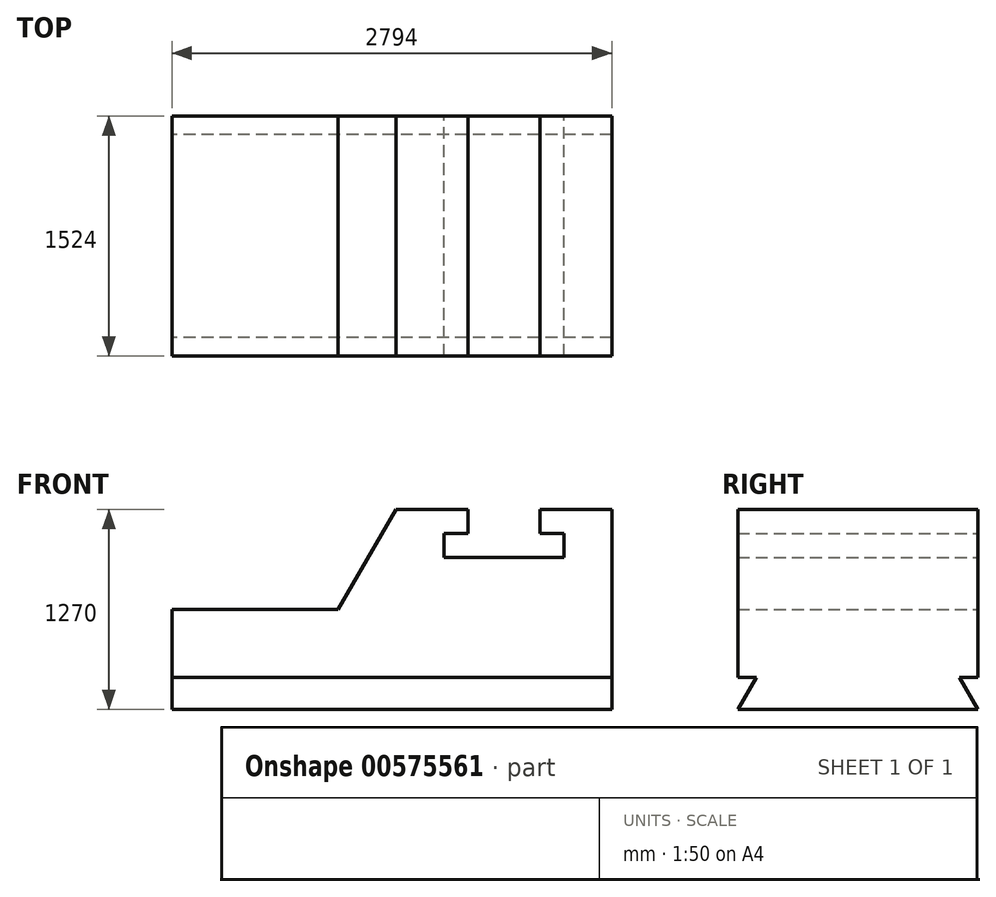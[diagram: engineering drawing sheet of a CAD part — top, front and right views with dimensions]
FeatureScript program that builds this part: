
annotation { "Feature Type Name" : "Feature", "Feature Type Description" : "" }
export const myFeature = defineFeature(function(context is Context, id is Id, definition is map)
    precondition{}
    {
        {
            var Q0;
            Q0=qCreatedBy(makeId("Front.planeOp"),FACE);
            var sketch = newSketch(context, id + "F0", { "sketchPlane" : qUnion([Q0])});
            skLineSegment(sketch, "E0", {"start": v(-53.89, -19.32) * mm, "end": v(2740.11, -19.32) * mm});
            skLineSegment(sketch, "E1", {"start": v(2740.11, -19.32) * mm, "end": v(2740.11, 1250.68) * mm});
            skLineSegment(sketch, "E2", {"start": v(2740.11, 1250.68) * mm, "end": v(2282.91, 1250.68) * mm});
            skLineSegment(sketch, "E3", {"start": v(2282.91, 1250.68) * mm, "end": v(2282.91, 1098.28) * mm});
            skLineSegment(sketch, "E4", {"start": v(2282.91, 1098.28) * mm, "end": v(2435.31, 1098.28) * mm});
            skLineSegment(sketch, "E5", {"start": v(2435.31, 1098.28) * mm, "end": v(2435.31, 945.88) * mm});
            skLineSegment(sketch, "E6", {"start": v(2435.31, 945.88) * mm, "end": v(1673.31, 945.88) * mm});
            skLineSegment(sketch, "E7", {"start": v(1673.31, 945.88) * mm, "end": v(1673.31, 1098.28) * mm});
            skLineSegment(sketch, "E8", {"start": v(1673.31, 1098.28) * mm, "end": v(1825.71, 1098.28) * mm});
            skLineSegment(sketch, "E9", {"start": v(1825.71, 1098.28) * mm, "end": v(1825.71, 1250.68) * mm});
            skLineSegment(sketch, "E10", {"start": v(1825.71, 1250.68) * mm, "end": v(1368.51, 1250.68) * mm});
            skLineSegment(sketch, "E11", {"start": v(-53.89, -19.32) * mm, "end": v(-53.89, 615.68) * mm});
            skLineSegment(sketch, "E12", {"start": v(1368.51, 1250.68) * mm, "end": v(1001.9, 615.68) * mm});
            skLineSegment(sketch, "E13", {"start": v(-53.89, 615.68) * mm, "end": v(1001.9, 615.68) * mm});
            skSolve(sketch);
        }
        {
            var Q0;
            Q0 = qSketchRegion(id + "F0", true);
            extrude(context, id + "F1", {"entities" : qUnion([Q0]), "depth" : 1524 * mm, "offsetDistance" : 25.4 * mm});
        }
        {
            var Q0;
            Q0=makeQuery(id+"F1.opExtrude","SWEPT_FACE",FACE,{"disambiguationData":[OSD([sQuery(id+"F0.wireOp",EDGE,"E11")])]});
            var sketch = newSketch(context, id + "F2", { "sketchPlane" : qUnion([Q0])});
            skLineSegment(sketch, "E14", {"start": v(0, -19.32) * mm, "end": v(0, 183.88) * mm});
            skLineSegment(sketch, "E15", {"start": v(0, -19.32) * mm, "end": v(117.32, 183.88) * mm});
            skLineSegment(sketch, "E16", {"start": v(117.32, 183.88) * mm, "end": v(0, 183.88) * mm});
            skSolve(sketch);
        }
        {
            var Q0;
            Q0 = qSketchRegion(id + "F2", true);
            extrude(context, id + "F3", {"entities" : qUnion([Q0]), "operationType" : NewBodyOperationType.REMOVE, "endBound" : BoundingType.THROUGH_ALL, "oppositeDirection" : true, "depth" : 25.4 * mm, "offsetDistance" : 25.4 * mm});
        }
        {
            var Q0;
            Q0=makeQuery(id+"F1.opExtrude","SWEPT_FACE",FACE,{"disambiguationData":[OSD([sQuery(id+"F0.wireOp",EDGE,"E11")])]});
            var sketch = newSketch(context, id + "F4", { "sketchPlane" : qUnion([Q0])});
            skLineSegment(sketch, "E17", {"start": v(1524, -19.32) * mm, "end": v(1524, 183.88) * mm});
            skLineSegment(sketch, "E18", {"start": v(1524, 183.88) * mm, "end": v(1406.68, 183.88) * mm});
            skLineSegment(sketch, "E19", {"start": v(1524, -19.32) * mm, "end": v(1406.68, 183.88) * mm});
            skSolve(sketch);
        }
        {
            var Q0;
            Q0=makeQuery(id+"F4.imprint","IMPRINT",FACE,{"disambiguationData":[TD([[makeQuery(id+"F4.imprint","IMPRINT",EDGE,{"derivedFrom":sQuery(id+"F4.wireOp",EDGE,"E17")}),1.0]])]});
            extrude(context, id + "F5", {"entities" : qUnion([Q0]), "operationType" : NewBodyOperationType.REMOVE, "endBound" : BoundingType.THROUGH_ALL, "oppositeDirection" : true, "depth" : 25.4 * mm, "offsetDistance" : 25.4 * mm});
        }
    });
